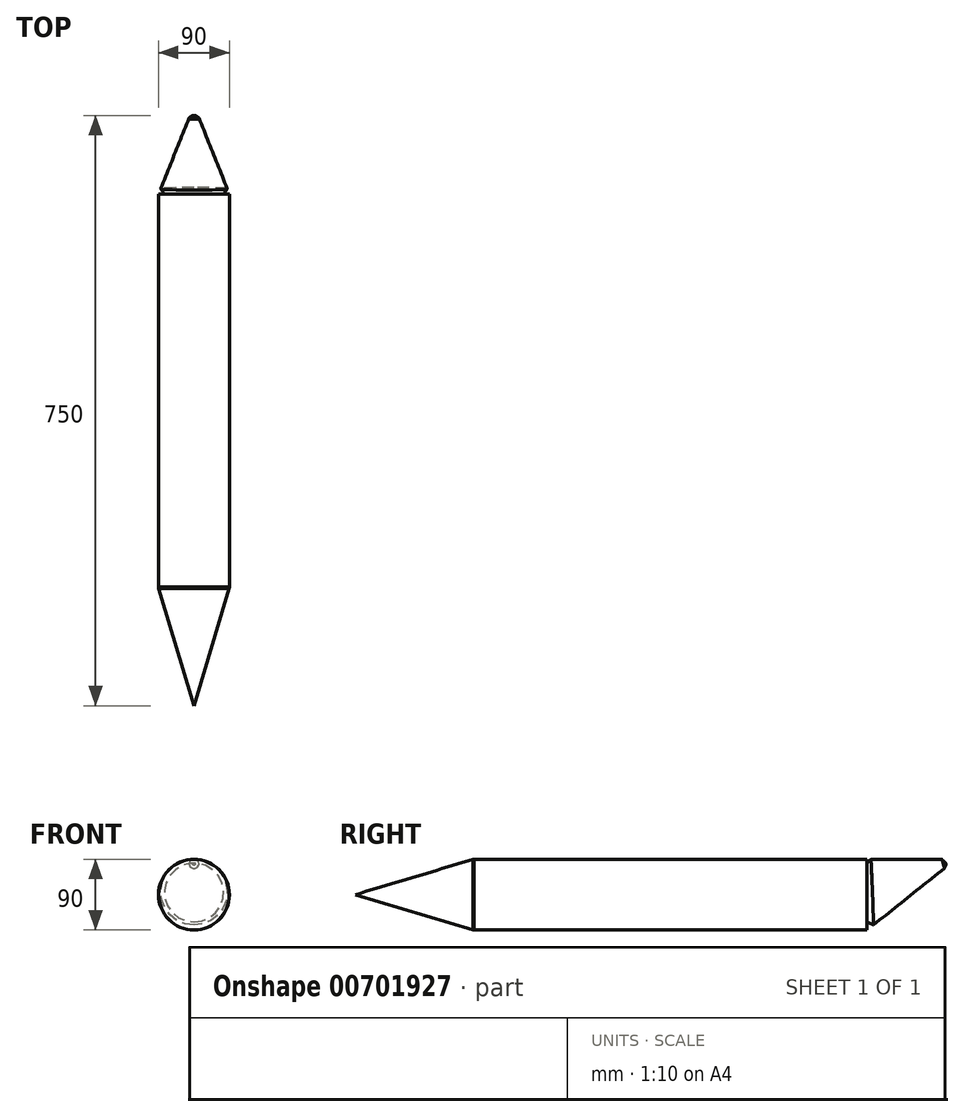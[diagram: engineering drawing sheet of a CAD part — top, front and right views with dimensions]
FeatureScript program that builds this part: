
annotation { "Feature Type Name" : "Feature", "Feature Type Description" : "" }
export const myFeature = defineFeature(function(context is Context, id is Id, definition is map)
    precondition{}
    {
        {
            var Q0;
            Q0=qCreatedBy(makeId("Front.planeOp"),FACE);
            var sketch = newSketch(context, id + "F0", { "sketchPlane" : qUnion([Q0])});
            skCircle(sketch, "E0", {"center": v(0, 0) * mm, "radius": 45 * mm});
            skSolve(sketch);
        }
        {
            var Q0;
            Q0=makeQuery(id+"F0.imprint","IMPRINT",FACE,{"disambiguationData":[TD([[makeQuery(id+"F0.imprint","IMPRINT",EDGE,{"derivedFrom":sQuery(id+"F0.wireOp",EDGE,"E0")}),1.0]])]});
            extrude(context, id + "F1", {"entities" : qUnion([Q0]), "endBound" : BoundingType.SYMMETRIC, "oppositeDirection" : true, "depth" : 500 * mm, "offsetDistance" : 25 * mm});
        }
        {
            var Q0;
            Q0=makeQuery(id+"F1.opExtrude","CAP_FACE",FACE,{"disambiguationData":[OSD([sQuery(id+"F0.wireOp",EDGE,"E0")])],"isStart":true});
            cPlane(context, id + "F2", {"entities" : qUnion([Q0]), "cplaneType" : CPlaneType.OFFSET, "offset" : 150 * mm, "width" : 150 * mm, "height" : 150 * mm});
        }
        {
            var Q0;
            Q0=qCreatedBy(id+"F2.planeOp",FACE);
            var sketch = newSketch(context, id + "F3", { "sketchPlane" : qUnion([Q0])});
            skCircle(sketch, "E1", {"center": v(0, 0) * mm, "radius": 2.5 * mm});
            skSolve(sketch);
        }
        {
            var Q1;
            Q1=makeQuery(id+"F1.opExtrude","CAP_FACE",FACE,{"disambiguationData":[OSD([sQuery(id+"F0.wireOp",EDGE,"E0")])],"isStart":true});
            var Q2;
            Q2=sQuery(id+"F3.wireOp",VERTEX,"E1.center");
            loft(context, id + "F4", {"operationType" : NewBodyOperationType.ADD, "sheetProfilesArray" : [{ "sheetProfileEntities" : qUnion([Q1]) }, { "sheetProfileEntities" : qUnion([Q2]) }]});
        }
        {
            var Q0;
            Q0=makeQuery(id+"F1.opExtrude","CAP_FACE",FACE,{"disambiguationData":[OSD([sQuery(id+"F0.wireOp",EDGE,"E0")])],"isStart":false});
            cPlane(context, id + "F5", {"entities" : qUnion([Q0]), "cplaneType" : CPlaneType.OFFSET, "offset" : 100 * mm, "width" : 150 * mm, "height" : 150 * mm});
        }
        {
            var Q0;
            Q0=qCreatedBy(id+"F5.planeOp",FACE);
            var sketch = newSketch(context, id + "F6", { "sketchPlane" : qUnion([Q0])});
            skLineSegment(sketch, "E2", {"start": v(0, 0) * mm, "end": v(0, 40) * mm, "construction": true});
            skCircle(sketch, "E3", {"center": v(0, 40) * mm, "radius": 5 * mm});
            skSolve(sketch);
        }
        {
            var Q0;
            Q0=makeQuery(id+"F1.opExtrude","CAP_FACE",FACE,{"disambiguationData":[OSD([sQuery(id+"F0.wireOp",EDGE,"E0")])],"isStart":false});
            var Q1;
            Q1=makeQuery(id+"F6.imprint","IMPRINT",FACE,{"disambiguationData":[TD([[makeQuery(id+"F6.imprint","IMPRINT",EDGE,{"derivedFrom":sQuery(id+"F6.wireOp",EDGE,"E3")}),1.0]])]});
            loft(context, id + "F7", {"sheetProfilesArray" : [{ "sheetProfileEntities" : qUnion([Q0]) }, { "sheetProfileEntities" : qUnion([Q1]) }]});
        }
        {
            var Q0;
            Q0=makeQuery(id+"F7.opLoft","MID_CAP_EDGE",EDGE,{"disambiguationData":[OSD([sQuery(id+"F0.wireOp",EDGE,"E0")])],"capPos":0.0});
            var Q1;
            Q1=makeQuery(id+"F7.opLoft","MID_CAP_EDGE",EDGE,{"disambiguationData":[OSD([sQuery(id+"F0.wireOp",EDGE,"E0"),sQuery(id+"F6.wireOp",EDGE,"E3")])],"capPos":1.0});
            var Q2;
            {var subQ0=sQuery(id+"F0.wireOp",EDGE,"E0");Q2=makeQuery(id+"F4.boolean.opBoolean","MERGE",EDGE,{"derivedFrom":[makeQuery(id+"F1.opExtrude","CAP_EDGE",EDGE,{"disambiguationData":[OSD([subQ0])],"isStart":true}),makeQuery(id+"F4.opLoft","MID_CAP_EDGE",EDGE,{"disambiguationData":[OSD([subQ0,sQuery(id+"F3.wireOp",VERTEX,"E1.center")])],"capPos":0.0})]});}
            chamfer(context, id + "F8", {"entities" : qUnion([Q0, Q1, Q2]), "width" : 5 * mm, "tangentPropagation" : true});
        }
    });
